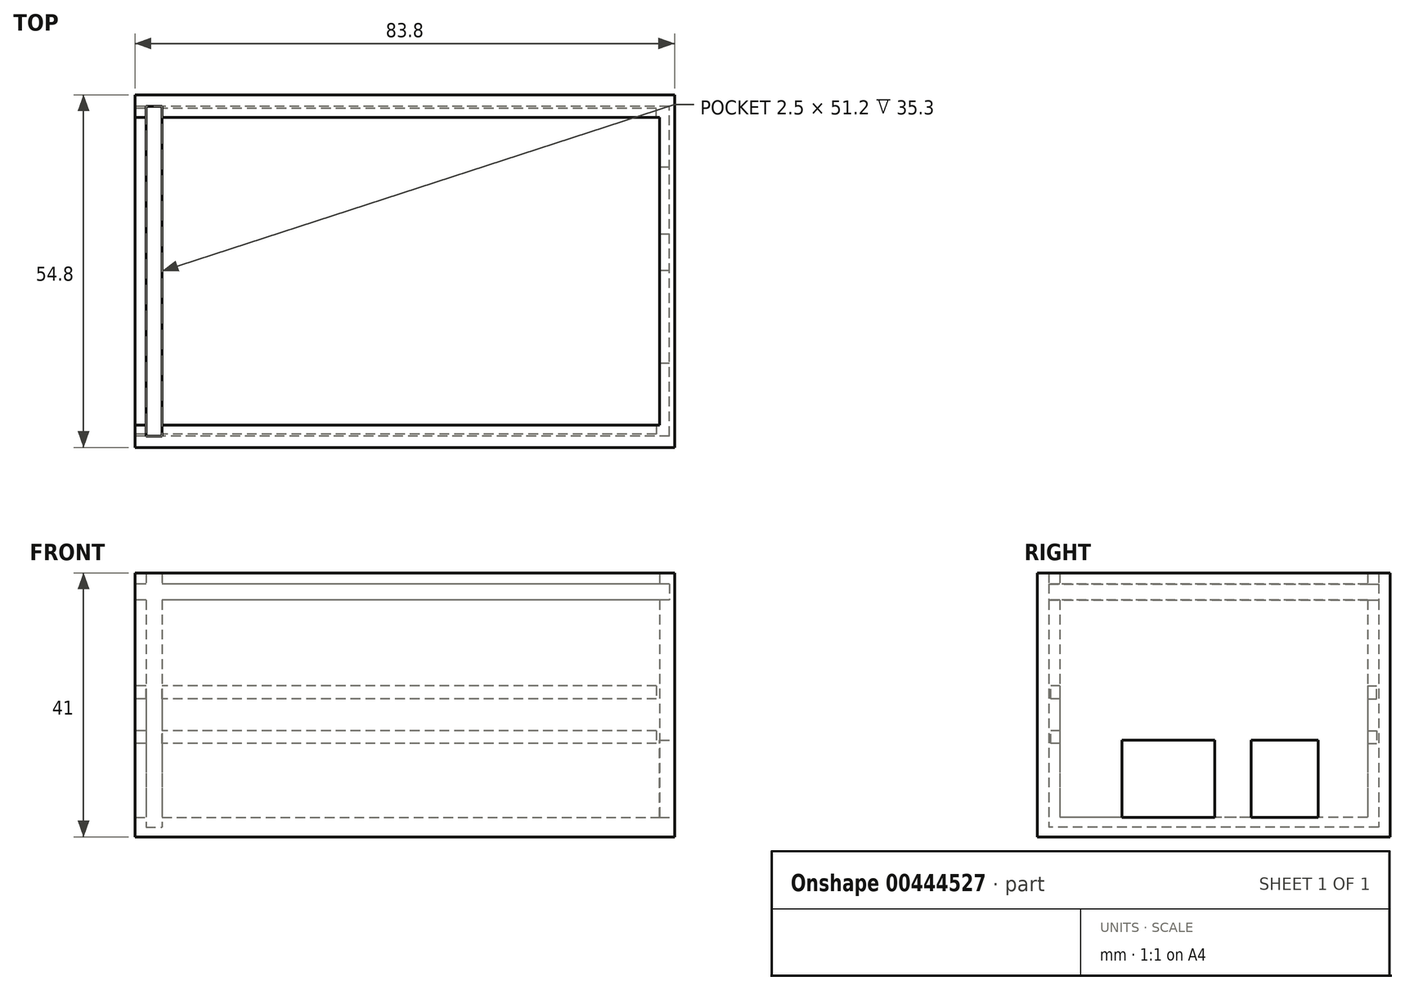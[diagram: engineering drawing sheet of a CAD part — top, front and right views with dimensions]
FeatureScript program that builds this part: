
annotation { "Feature Type Name" : "Feature", "Feature Type Description" : "" }
export const myFeature = defineFeature(function(context is Context, id is Id, definition is map)
    precondition{}
    {
        {
            var Q0;
            Q0=qCreatedBy(makeId("Top.planeOp"),FACE);
            var sketch = newSketch(context, id + "F0", { "sketchPlane" : qUnion([Q0])});
            skLineSegment(sketch, "E0.bottom", {"start": v(37.5, 25) * mm, "end": v(-37.5, 25) * mm, "construction": true});
            skLineSegment(sketch, "E0.top", {"start": v(37.5, -25) * mm, "end": v(-37.5, -25) * mm, "construction": true});
            skLineSegment(sketch, "E0.left", {"start": v(37.5, 25) * mm, "end": v(37.5, -25) * mm, "construction": true});
            skLineSegment(sketch, "E0.right", {"start": v(-37.5, 25) * mm, "end": v(-37.5, -25) * mm, "construction": true});
            skPoint(sketch, "E0.middle", {"position": v(0, 0) * mm});
            skCircle(sketch, "E1", {"center": v(-34.5, 22) * mm, "radius": 1.25 * mm, "construction": true});
            skCircle(sketch, "E2", {"center": v(-34.5, -22) * mm, "radius": 1.25 * mm, "construction": true});
            skCircle(sketch, "E3", {"center": v(34.5, -22) * mm, "radius": 1.25 * mm, "construction": true});
            skCircle(sketch, "E4", {"center": v(34.5, 22) * mm, "radius": 1.25 * mm, "construction": true});
            skLineSegment(sketch, "E5", {"start": v(37.5, -13.77) * mm, "end": v(41.3, -13.77) * mm, "construction": true});
            skLineSegment(sketch, "E6.left", {"start": v(37.5, -13.77) * mm, "end": v(37.5, -13.77) * mm});
            skLineSegment(sketch, "E6.right", {"start": v(41.3, -13.77) * mm, "end": v(41.3, -13.77) * mm});
            skLineSegment(sketch, "E7.top", {"start": v(37.5, -0.36) * mm, "end": v(41.3, -0.36) * mm, "construction": true});
            skLineSegment(sketch, "E7.left", {"start": v(37.5, -13.77) * mm, "end": v(37.5, -0.36) * mm, "construction": true});
            skLineSegment(sketch, "E7.right", {"start": v(41.3, -13.77) * mm, "end": v(41.3, -0.36) * mm, "construction": true});
            skLineSegment(sketch, "E8.bottom", {"start": v(37.5, 6.5) * mm, "end": v(41.3, 6.5) * mm, "construction": true});
            skLineSegment(sketch, "E8.top", {"start": v(37.5, 15.5) * mm, "end": v(41.3, 15.5) * mm, "construction": true});
            skLineSegment(sketch, "E8.left", {"start": v(37.5, 6.5) * mm, "end": v(37.5, 15.5) * mm, "construction": true});
            skLineSegment(sketch, "E8.right", {"start": v(41.3, 6.5) * mm, "end": v(41.3, 15.5) * mm, "construction": true});
            skSolve(sketch);
        }
        {
            var Q0;
            Q0=qCreatedBy(makeId("Top.planeOp"),FACE);
            var sketch = newSketch(context, id + "F1", { "sketchPlane" : qUnion([Q0])});
            skLineSegment(sketch, "E9.bottom", {"start": v(-43, 23.9) * mm, "end": v(38.5, 23.9) * mm});
            skLineSegment(sketch, "E9.top", {"start": v(-43, -23.9) * mm, "end": v(38.5, -23.9) * mm});
            skLineSegment(sketch, "E9.left", {"start": v(-43, 23.9) * mm, "end": v(-43, -23.9) * mm});
            skLineSegment(sketch, "E9.right", {"start": v(38.5, 23.9) * mm, "end": v(38.5, -23.9) * mm});
            skLineSegment(sketch, "E10.bottom", {"start": v(-43, 27.4) * mm, "end": v(40.8, 27.4) * mm});
            skLineSegment(sketch, "E10.top", {"start": v(-43, -27.4) * mm, "end": v(40.8, -27.4) * mm});
            skLineSegment(sketch, "E10.left", {"start": v(-43, 27.4) * mm, "end": v(-43, -27.4) * mm});
            skLineSegment(sketch, "E10.right", {"start": v(40.8, 27.4) * mm, "end": v(40.8, -27.4) * mm});
            skLineSegment(sketch, "E11.bottom", {"start": v(-41.3, -23.9) * mm, "end": v(-38.8, -23.9) * mm});
            skLineSegment(sketch, "E11.top", {"start": v(-41.3, -25.6) * mm, "end": v(-38.8, -25.6) * mm});
            skLineSegment(sketch, "E11.left", {"start": v(-41.3, -23.9) * mm, "end": v(-41.3, -25.6) * mm});
            skLineSegment(sketch, "E11.right", {"start": v(-38.8, -23.9) * mm, "end": v(-38.8, -25.6) * mm});
            skLineSegment(sketch, "E12.bottom", {"start": v(-41.3, 23.9) * mm, "end": v(-38.8, 23.9) * mm});
            skLineSegment(sketch, "E12.top", {"start": v(-41.3, 25.6) * mm, "end": v(-38.8, 25.6) * mm});
            skLineSegment(sketch, "E12.left", {"start": v(-41.3, 23.9) * mm, "end": v(-41.3, 25.6) * mm});
            skLineSegment(sketch, "E12.right", {"start": v(-38.8, 23.9) * mm, "end": v(-38.8, 25.6) * mm});
            skLineSegment(sketch, "E13.left", {"start": v(-41.3, 23.9) * mm, "end": v(-41.3, -23.9) * mm});
            skLineSegment(sketch, "E13.right", {"start": v(-38.8, 23.9) * mm, "end": v(-38.8, -23.9) * mm});
            skSolve(sketch);
        }
        {
            var Q0;
            {var subQ6=sQuery(id+"F1.wireOp",EDGE,"E9.right");Q0=makeQuery(id+"F1.imprint","IMPRINT",FACE,{"disambiguationData":[TD([[makeQuery(id+"F1.imprint","IMPRINT",EDGE,{"derivedFrom":subQ6}),1.0]])]});}
            extrude(context, id + "F2", {"entities" : qUnion([Q0]), "depth" : 41 * mm});
        }
        {
            var Q0;
            {var subQ2=sQuery(id+"F1.wireOp",EDGE,"E9.right");Q0=makeQuery(id+"F1.imprint","IMPRINT",FACE,{"disambiguationData":[TD([[makeQuery(id+"F1.imprint","IMPRINT",EDGE,{"derivedFrom":subQ2}),-1.0]])]});}
            var Q1;
            Q1=makeQuery(id+"F1.imprint","IMPRINT",FACE,{"disambiguationData":[TD([[makeQuery(id+"F1.imprint","IMPRINT",EDGE,{"derivedFrom":sQuery(id+"F1.wireOp",EDGE,"E12.bottom")}),1.0]])]});
            var Q2;
            Q2=makeQuery(id+"F1.imprint","IMPRINT",FACE,{"disambiguationData":[TD([[makeQuery(id+"F1.imprint","IMPRINT",EDGE,{"derivedFrom":sQuery(id+"F1.wireOp",EDGE,"E11.bottom")}),-1.0]])]});
            var Q3;
            {var subQ3=sQuery(id+"F1.wireOp",EDGE,"E9.left");Q3=makeQuery(id+"F1.imprint","IMPRINT",FACE,{"disambiguationData":[TD([[makeQuery(id+"F1.imprint","IMPRINT",EDGE,{"derivedFrom":subQ3}),1.0]])]});}
            extrude(context, id + "F3", {"entities" : qUnion([Q0, Q1, Q2, Q3]), "operationType" : NewBodyOperationType.ADD, "depth" : 3 * mm});
        }
        {
            var Q0;
            Q0=makeQuery(id+"F1.imprint","IMPRINT",FACE,{"disambiguationData":[TD([[makeQuery(id+"F1.imprint","IMPRINT",EDGE,{"derivedFrom":sQuery(id+"F1.wireOp",EDGE,"E11.top")}),1.0]])]});
            var Q1;
            {var subQ2=sQuery(id+"F1.wireOp",EDGE,"E13.left");Q1=makeQuery(id+"F1.imprint","IMPRINT",FACE,{"disambiguationData":[TD([[makeQuery(id+"F1.imprint","IMPRINT",EDGE,{"derivedFrom":subQ2}),1.0]])]});}
            var Q2;
            Q2=makeQuery(id+"F1.imprint","IMPRINT",FACE,{"disambiguationData":[TD([[makeQuery(id+"F1.imprint","IMPRINT",EDGE,{"derivedFrom":sQuery(id+"F1.wireOp",EDGE,"E12.top")}),-1.0]])]});
            extrude(context, id + "F4", {"entities" : qUnion([Q0, Q1, Q2]), "operationType" : NewBodyOperationType.ADD, "depth" : 1.5 * mm});
        }
        {
            var Q0;
            Q0=makeQuery(id+"F2.opExtrude","SWEPT_FACE",FACE,{"disambiguationData":[OSD([sQuery(id+"F1.wireOp",EDGE,"E10.right")])]});
            var sketch = newSketch(context, id + "F5", { "sketchPlane" : qUnion([Q0])});
            skPoint(sketch, "E14.0", {"position": v(-13.77, 0) * mm});
            skPoint(sketch, "E15.0", {"position": v(-0.36, 0) * mm});
            skPoint(sketch, "E16.0", {"position": v(6.5, 0) * mm});
            skPoint(sketch, "E17.0", {"position": v(15.5, 0) * mm});
            skLineSegment(sketch, "E18.bottom", {"start": v(-0.36, 0) * mm, "end": v(-13.77, 0) * mm, "construction": true});
            skLineSegment(sketch, "E18.top", {"start": v(-0.36, 14) * mm, "end": v(-13.77, 14) * mm, "construction": true});
            skLineSegment(sketch, "E18.left", {"start": v(-0.36, 0) * mm, "end": v(-0.36, 14) * mm, "construction": true});
            skLineSegment(sketch, "E18.right", {"start": v(-13.77, 0) * mm, "end": v(-13.77, 14) * mm, "construction": true});
            skLineSegment(sketch, "E19.bottom", {"start": v(6.5, 0) * mm, "end": v(15.5, 0) * mm, "construction": true});
            skLineSegment(sketch, "E19.top", {"start": v(6.5, 14) * mm, "end": v(15.5, 14) * mm, "construction": true});
            skLineSegment(sketch, "E19.left", {"start": v(6.5, 0) * mm, "end": v(6.5, 14) * mm, "construction": true});
            skLineSegment(sketch, "E19.right", {"start": v(15.5, 0) * mm, "end": v(15.5, 14) * mm, "construction": true});
            skLineSegment(sketch, "E20.bottom", {"start": v(-14.27, 0) * mm, "end": v(0.14, 0) * mm});
            skLineSegment(sketch, "E20.top", {"start": v(-14.27, 15) * mm, "end": v(0.14, 15) * mm});
            skLineSegment(sketch, "E20.left", {"start": v(-14.27, 0) * mm, "end": v(-14.27, 15) * mm});
            skLineSegment(sketch, "E20.right", {"start": v(0.14, 0) * mm, "end": v(0.14, 15) * mm});
            skLineSegment(sketch, "E21.bottom", {"start": v(5.8, 0) * mm, "end": v(16.2, 0) * mm});
            skLineSegment(sketch, "E21.top", {"start": v(5.8, 15) * mm, "end": v(16.2, 15) * mm});
            skLineSegment(sketch, "E21.left", {"start": v(5.8, 0) * mm, "end": v(5.8, 15) * mm});
            skLineSegment(sketch, "E21.right", {"start": v(16.2, 0) * mm, "end": v(16.2, 15) * mm});
            skLineSegment(sketch, "E22.top", {"start": v(-14.27, 3) * mm, "end": v(0.14, 3) * mm});
            skLineSegment(sketch, "E22.left", {"start": v(-14.27, 0) * mm, "end": v(-14.27, 3) * mm});
            skLineSegment(sketch, "E22.right", {"start": v(0.14, 0) * mm, "end": v(0.14, 3) * mm});
            skLineSegment(sketch, "E23.top", {"start": v(5.8, 3) * mm, "end": v(16.2, 3) * mm});
            skLineSegment(sketch, "E23.left", {"start": v(5.8, 0) * mm, "end": v(5.8, 3) * mm});
            skLineSegment(sketch, "E23.right", {"start": v(16.2, 0) * mm, "end": v(16.2, 3) * mm});
            skSolve(sketch);
        }
        {
            var Q0;
            Q0=makeQuery(id+"F5.imprint","IMPRINT",FACE,{"disambiguationData":[TD([[makeQuery(id+"F5.imprint","IMPRINT",EDGE,{"derivedFrom":sQuery(id+"F5.wireOp",EDGE,"E20.top")}),-1.0]])]});
            var Q1;
            Q1=makeQuery(id+"F5.imprint","IMPRINT",FACE,{"disambiguationData":[TD([[makeQuery(id+"F5.imprint","IMPRINT",EDGE,{"derivedFrom":sQuery(id+"F5.wireOp",EDGE,"E21.top")}),-1.0]])]});
            extrude(context, id + "F6", {"entities" : qUnion([Q0, Q1]), "operationType" : NewBodyOperationType.REMOVE, "oppositeDirection" : true, "depth" : 3 * mm});
        }
        {
            var Q0;
            {var subQ0=sQuery(id+"F1.wireOp",EDGE,"E9.left");var subQ1=sQuery(id+"F1.wireOp",EDGE,"E10.left");Q0=makeQuery(id+"F3.boolean.opBoolean","MERGE",FACE,{"derivedFrom":[makeQuery(id+"F2.opExtrude","SWEPT_FACE",FACE,{"disambiguationData":[OSD([subQ1]),TDD([makeQuery(id+"F1.imprint","IMPRINT",EDGE,{"disambiguationData":[TD([[makeQuery(id+"F1.imprint","INTERSECT",VERTEX,{"derivedFrom":[sQuery(id+"F1.wireOp",EDGE,"E10.top"),subQ1]}),1.0]])],"derivedFrom":subQ1})])]}),makeQuery(id+"F2.opExtrude","SWEPT_FACE",FACE,{"disambiguationData":[OSD([subQ1]),TDD([makeQuery(id+"F1.imprint","IMPRINT",EDGE,{"disambiguationData":[TD([[makeQuery(id+"F1.imprint","INTERSECT",VERTEX,{"derivedFrom":[sQuery(id+"F1.wireOp",EDGE,"E10.bottom"),subQ1]}),-1.0]])],"derivedFrom":subQ1})])]}),makeQuery(id+"F3.opExtrude","SWEPT_FACE",FACE,{"disambiguationData":[OSD([subQ0])]})]});}
            var sketch = newSketch(context, id + "F7", { "sketchPlane" : qUnion([Q0])});
            skLineSegment(sketch, "E24.bottom", {"start": v(-23.9, 16.5) * mm, "end": v(-25.3, 16.5) * mm});
            skLineSegment(sketch, "E24.top", {"start": v(-23.9, 14.5) * mm, "end": v(-25.3, 14.5) * mm});
            skLineSegment(sketch, "E24.left", {"start": v(-23.9, 16.5) * mm, "end": v(-23.9, 14.5) * mm});
            skLineSegment(sketch, "E24.right", {"start": v(-25.3, 16.5) * mm, "end": v(-25.3, 14.5) * mm});
            skLineSegment(sketch, "E25.bottom", {"start": v(23.9, 14.5) * mm, "end": v(25.3, 14.5) * mm});
            skLineSegment(sketch, "E25.top", {"start": v(23.9, 16.5) * mm, "end": v(25.3, 16.5) * mm});
            skLineSegment(sketch, "E25.left", {"start": v(23.9, 14.5) * mm, "end": v(23.9, 16.5) * mm});
            skLineSegment(sketch, "E25.right", {"start": v(25.3, 14.5) * mm, "end": v(25.3, 16.5) * mm});
            skLineSegment(sketch, "E26.bottom", {"start": v(-23.9, 21.45) * mm, "end": v(-25.3, 21.45) * mm});
            skLineSegment(sketch, "E26.top", {"start": v(-23.9, 23.45) * mm, "end": v(-25.3, 23.45) * mm});
            skLineSegment(sketch, "E26.left", {"start": v(-23.9, 21.45) * mm, "end": v(-23.9, 23.45) * mm});
            skLineSegment(sketch, "E26.right", {"start": v(-25.3, 21.45) * mm, "end": v(-25.3, 23.45) * mm});
            skLineSegment(sketch, "E27.bottom", {"start": v(23.9, 21.45) * mm, "end": v(25.3, 21.45) * mm});
            skLineSegment(sketch, "E27.top", {"start": v(23.9, 23.45) * mm, "end": v(25.3, 23.45) * mm});
            skLineSegment(sketch, "E27.left", {"start": v(23.9, 21.45) * mm, "end": v(23.9, 23.45) * mm});
            skLineSegment(sketch, "E27.right", {"start": v(25.3, 21.45) * mm, "end": v(25.3, 23.45) * mm});
            skSolve(sketch);
        }
        {
            var Q0;
            Q0=makeQuery(id+"F7.imprint","IMPRINT",FACE,{"disambiguationData":[TD([[makeQuery(id+"F7.imprint","IMPRINT",EDGE,{"derivedFrom":sQuery(id+"F7.wireOp",EDGE,"E24.bottom")}),1.0]])]});
            var Q1;
            Q1=makeQuery(id+"F7.imprint","IMPRINT",FACE,{"disambiguationData":[TD([[makeQuery(id+"F7.imprint","IMPRINT",EDGE,{"derivedFrom":sQuery(id+"F7.wireOp",EDGE,"E26.bottom")}),-1.0]])]});
            var Q2;
            Q2=makeQuery(id+"F7.imprint","IMPRINT",FACE,{"disambiguationData":[TD([[makeQuery(id+"F7.imprint","IMPRINT",EDGE,{"derivedFrom":sQuery(id+"F7.wireOp",EDGE,"E25.bottom")}),1.0]])]});
            var Q3;
            Q3=makeQuery(id+"F7.imprint","IMPRINT",FACE,{"disambiguationData":[TD([[makeQuery(id+"F7.imprint","IMPRINT",EDGE,{"derivedFrom":sQuery(id+"F7.wireOp",EDGE,"E27.bottom")}),1.0]])]});
            extrude(context, id + "F8", {"entities" : qUnion([Q0, Q1, Q2, Q3]), "operationType" : NewBodyOperationType.REMOVE, "oppositeDirection" : true, "depth" : 81 * mm});
        }
        {
            var Q0;
            {var subQ0=sQuery(id+"F1.wireOp",EDGE,"E9.left");var subQ1=sQuery(id+"F1.wireOp",EDGE,"E10.left");Q0=makeQuery(id+"F3.boolean.opBoolean","MERGE",FACE,{"derivedFrom":[makeQuery(id+"F2.opExtrude","SWEPT_FACE",FACE,{"disambiguationData":[OSD([subQ1]),TDD([makeQuery(id+"F1.imprint","IMPRINT",EDGE,{"disambiguationData":[TD([[makeQuery(id+"F1.imprint","INTERSECT",VERTEX,{"derivedFrom":[sQuery(id+"F1.wireOp",EDGE,"E10.top"),subQ1]}),1.0]])],"derivedFrom":subQ1})])]}),makeQuery(id+"F2.opExtrude","SWEPT_FACE",FACE,{"disambiguationData":[OSD([subQ1]),TDD([makeQuery(id+"F1.imprint","IMPRINT",EDGE,{"disambiguationData":[TD([[makeQuery(id+"F1.imprint","INTERSECT",VERTEX,{"derivedFrom":[sQuery(id+"F1.wireOp",EDGE,"E10.bottom"),subQ1]}),-1.0]])],"derivedFrom":subQ1})])]}),makeQuery(id+"F3.opExtrude","SWEPT_FACE",FACE,{"disambiguationData":[OSD([subQ0])]})]});}
            var sketch = newSketch(context, id + "F9", { "sketchPlane" : qUnion([Q0])});
            skLineSegment(sketch, "E28.bottom", {"start": v(-23.9, 39.3) * mm, "end": v(-25.6, 39.3) * mm});
            skLineSegment(sketch, "E28.top", {"start": v(-23.9, 36.8) * mm, "end": v(-25.6, 36.8) * mm});
            skLineSegment(sketch, "E28.left", {"start": v(-23.9, 39.3) * mm, "end": v(-23.9, 36.8) * mm});
            skLineSegment(sketch, "E28.right", {"start": v(-25.6, 39.3) * mm, "end": v(-25.6, 36.8) * mm});
            skLineSegment(sketch, "E29.bottom", {"start": v(23.9, 39.3) * mm, "end": v(25.6, 39.3) * mm});
            skLineSegment(sketch, "E29.top", {"start": v(23.9, 36.8) * mm, "end": v(25.6, 36.8) * mm});
            skLineSegment(sketch, "E29.left", {"start": v(23.9, 39.3) * mm, "end": v(23.9, 36.8) * mm});
            skLineSegment(sketch, "E29.right", {"start": v(25.6, 39.3) * mm, "end": v(25.6, 36.8) * mm});
            skSolve(sketch);
        }
        {
            var Q0;
            Q0=makeQuery(id+"F9.imprint","IMPRINT",FACE,{"disambiguationData":[TD([[makeQuery(id+"F9.imprint","IMPRINT",EDGE,{"derivedFrom":sQuery(id+"F9.wireOp",EDGE,"E28.bottom")}),1.0]])]});
            var Q1;
            Q1=makeQuery(id+"F9.imprint","IMPRINT",FACE,{"disambiguationData":[TD([[makeQuery(id+"F9.imprint","IMPRINT",EDGE,{"derivedFrom":sQuery(id+"F9.wireOp",EDGE,"E29.bottom")}),-1.0]])]});
            extrude(context, id + "F10", {"entities" : qUnion([Q0, Q1]), "operationType" : NewBodyOperationType.REMOVE, "oppositeDirection" : true, "depth" : 83 * mm});
        }
        {
            var Q0;
            Q0=makeQuery(id+"F2.opExtrude","SWEPT_FACE",FACE,{"disambiguationData":[OSD([sQuery(id+"F1.wireOp",EDGE,"E9.right")])]});
            var sketch = newSketch(context, id + "F11", { "sketchPlane" : qUnion([Q0])});
            skLineSegment(sketch, "E30.bottom", {"start": v(-23.9, 39.3) * mm, "end": v(23.9, 39.3) * mm});
            skLineSegment(sketch, "E30.top", {"start": v(-23.9, 36.8) * mm, "end": v(23.9, 36.8) * mm});
            skLineSegment(sketch, "E30.left", {"start": v(-23.9, 39.3) * mm, "end": v(-23.9, 36.8) * mm});
            skLineSegment(sketch, "E30.right", {"start": v(23.9, 39.3) * mm, "end": v(23.9, 36.8) * mm});
            skSolve(sketch);
        }
        {
            var Q0;
            Q0=makeQuery(id+"F11.imprint","IMPRINT",FACE,{"disambiguationData":[TD([[makeQuery(id+"F11.imprint","IMPRINT",EDGE,{"derivedFrom":sQuery(id+"F11.wireOp",EDGE,"E30.bottom")}),-1.0]])]});
            extrude(context, id + "F12", {"entities" : qUnion([Q0]), "operationType" : NewBodyOperationType.REMOVE, "oppositeDirection" : true, "depth" : 1.5 * mm});
        }
    });
